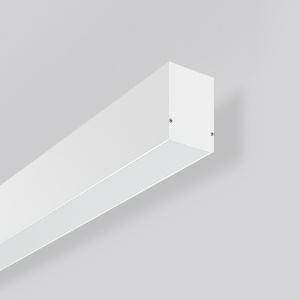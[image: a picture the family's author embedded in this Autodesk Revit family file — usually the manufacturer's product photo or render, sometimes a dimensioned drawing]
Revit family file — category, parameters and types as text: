
# Revit family: less_is_more_50_312606_002_1_76_6011
name_source: partatom
category: Lighting Fixtures
units: mm (PartAtom-declared; Revit-internal decimal feet)

## family parameters
Cut with Voids When Loaded = No
Host = Face
Light Source = No
Part Type = Normal
Room Calculation Point = No
Round Connector Dimension = Use Diameter
Shared = No

## types (1)
- LESS IS MORE 50 (1 x LED Modul 840, 2050 lm, 4000)
    Apparent Load = 16 VA
    CIE Flux Codes = 48 80 96 50 100
    Color Rendering = 80
    Color Temperature = 4000
    Default Elevation = 1800 mm
    Description = Series: LESS IS MORE 50
Linear wall luminaires. Housing: extruded aluminium profile, powder-coated. End cap aluminium powder-coated. Diffuser made of non-yellowing plastic (PMMA), opal. Direct 50%, indirect 50% light emission. Suitable for Wall (surface). LED unit with integrated converter interchangeable and removable. Suitable for through-wiring. With sensors or as a safety luminaire on request. 
Colour: traffic white, matt (RAL 9016)
Length: 847 mm
Width: 67 mm
Height: 75 mm
Lamp: LED
Socket: without socket
Colour temperature: 4000K
Colour rendering index (CRI): 80
Light source: LED
Socket lamp2: Without base
Colour temperature: 4000K
Colour rendering index (CRI) 2: 80
System power: 16 W
Rated luminous flux: 2050 lm
Luminous efficiency: 128 lm/W
Control gear: Converter, dimmable, DALI
Control gear: Converter, dimmable, DALI
Protection class: I
Type of protection: IP 20
    Height = 75 mm
    Lamp = 1 x LED Modul 840
    Lamp Light Flux = 2050 lm
    Lamp count = 1
    Length = 847 mm
    Lifetime = 50000 h
    Luminous efficacy = 128 lm/W
    Manufacturer = RZB
    ModVariant = No
    Model = 312606.002.1.76
    Mounting Place = Wall
    Mounting Type = Surface mounted
    Number of Poles = 1
    OnlyDefault = Yes
    Power Factor = 1
    Product Name = LESS IS MORE 50
    Product group = Surface mounted LED linear luminaires
    ProductGroupID = 2007
    Protection Class = Protection class I
    Protection Degree = IP 20
    RLX_Detail_Level = 1
    RLX_Emergency_Light_Flux = 0 lm
    RLX_Emergency_Type = 0
    RLX_Emergency_Type_DB = No
    RlxData = <blob elided: 39565 chars, md5=38b51c47>
    Socket = socket
    Standby Power = 0 W
    System Light Flux = 2050 lm
    System Power = 16 W
    Type Comments = Product without accessories
    Type Image = 312606.002.jpg
    URL = http://relux.com
    VarID = ---
    Voltage = 0 V
    Weight = 0.00 kg
    Width = 67 mm

## geometry (parser evidence)
native form markers: Blend x4, Sweep x14
no freeform markers — native parametric forms only
